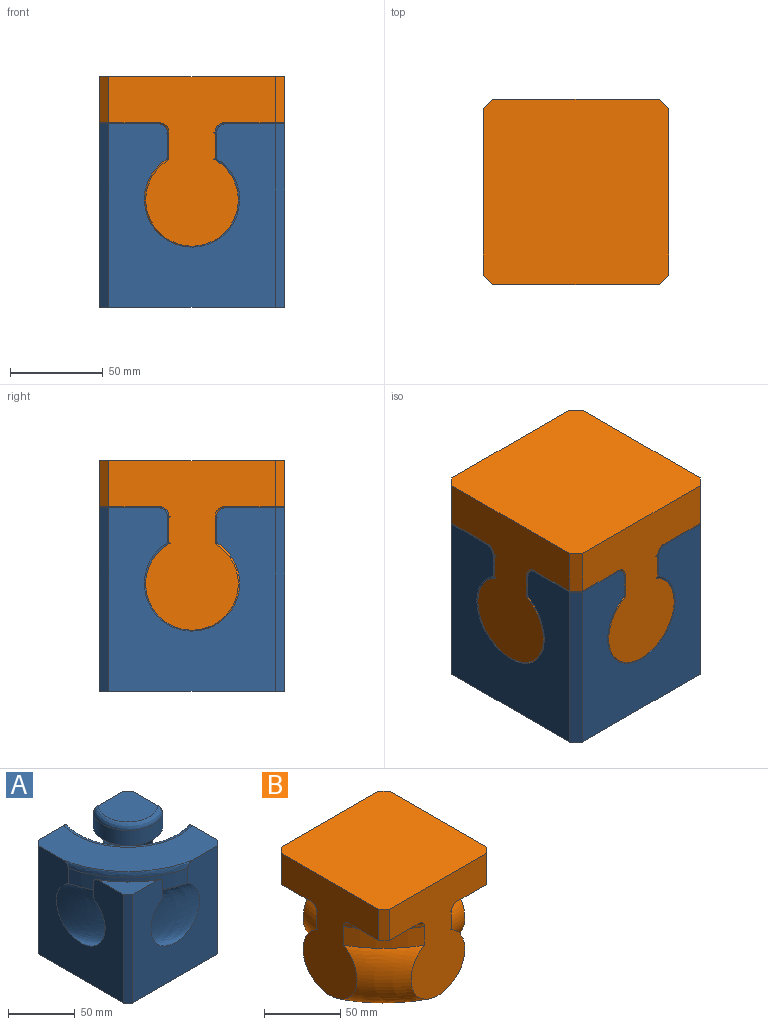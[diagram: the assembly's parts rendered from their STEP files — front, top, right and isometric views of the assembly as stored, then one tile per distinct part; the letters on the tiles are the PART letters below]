
ASSEMBLY  parts=2 mates=1
PART A: 23 faces, bbox 119.4x147.5x99.3 mm
  f0: plane 99.25x90mm, normal (0,1,0), area 6407.5mm2, adj f2,f10,f11,f12,f13,f14,f15,f16
  f1: plane 99.25x90mm, normal (0,-1,0), area 6405.8mm2, adj f2,f5,f6,f7,f8,f9,f17,f18
  f2: plane 100x100mm, normal (0,0,-1), area 9950mm2, adj f0,f1,f3,f4,f19,f20,f21,f22
  f3: plane 99.25x90mm, normal (1,0,0), area 6405.8mm2, adj f2,f10,f11,f12,f14,f15,f16,f17
  f4: plane 99.25x90mm, normal (-1,0,0), area 6405.9mm2, adj f2,f5,f6,f7,f8,f9,f17,f18
  f5: revolved ~41.04x39.31mm, area 308mm2, adj f1,f4,f6,f18
  f6: cylinder r=97.74mm len=36.75mm, axis (0,0,1), area 727.1mm2, adj f1,f4,f5,f7
  f7: revolved ~126.01x95.15mm, area 7683.8mm2, adj f1,f4,f6,f8
  f8: cylinder r=87.74mm len=63.25mm, axis (0,0,1), area 1297.3mm2, adj f1,f4,f7,f9
  f9: revolved ~72.88x70.15mm, area 505.8mm2, adj f1,f4,f8,f17
  f10: revolved ~73.16x70.32mm, area 865.8mm2, adj f0,f3,f11,f17
  f11: cylinder r=50.53mm len=65.53mm, axis (0,0,1), area 1518mm2, adj f0,f3,f10,f12
  f12: revolved ~125.04x77.52mm, area 12006mm2, adj f0,f3,f11,f13,f14
  f13: plane 7.92x0.28mm, normal (-0.91,0.42,0), area 1.6mm2, adj f0,f12
  f14: cylinder r=26.42mm len=41.42mm, axis (0,0,1), area 1014.5mm2, adj f0,f3,f12,f15
  f15: revolved ~46.37x41.42mm, area 502.3mm2, adj f0,f3,f14,f16
  f16: plane 37.48x37.48mm, normal (0,0,1), area 1230mm2, adj f0,f3,f15,f21
  f17: plane 100x100mm, normal (0,0,1), area 4340.4mm2, adj f0,f1,f3,f4,f9,f10,f20,f22
  f18: plane 31.75x31.75mm, normal (0,0,1), area 415.2mm2, adj f1,f4,f5,f19
  f19: plane 99.25x5mm, normal (-0.71,-0.71,0), area 701.8mm2, adj f1,f2,f4,f18
  f20: plane 99.25x5mm, normal (-0.71,0.71,0), area 701.8mm2, adj f0,f2,f4,f17
  f21: plane 99.25x5mm, normal (0.71,0.71,0), area 701.8mm2, adj f0,f2,f3,f16
  f22: plane 99.25x5mm, normal (0.71,-0.71,0), area 701.8mm2, adj f1,f2,f3,f17
PART B: 29 faces, bbox 119x146.8x91.7 mm
  f0: cylinder r=27.04mm len=18.52mm, axis (0,0,1), area 291.5mm2, adj f1,f4,f20,f27
  f1: revolved ~24.31x9.54mm, area 142mm2, adj f0,f17,f20,f27
  f2: revolved ~21.82x7.1mm, area 157.7mm2, adj f3,f15,f20,f27
  f3: cylinder r=49.81mm len=19.49mm, axis (0,0,1), area 296mm2, adj f2,f4,f20,f27
  f4: revolved ~75.55x51.74mm, area 2899mm2, adj f0,f3,f20,f27
  f5: revolved ~123.59x93.96mm, area 7490.6mm2, adj f7,f8,f16,f18
  f6: revolved ~41.76x40.12mm, area 313.9mm2, adj f7,f16,f18,f19
  f7: cylinder r=97.37mm len=37.5mm, axis (0,0,1), area 805.7mm2, adj f5,f6,f16,f18
  f8: cylinder r=87.93mm len=62.5mm, axis (0,0,1), area 1389.2mm2, adj f5,f9,f16,f18
  f9: revolved ~72.09x69.48mm, area 500.9mm2, adj f8,f15,f16,f18
  f10: cylinder r=27.04mm len=19.93mm, axis (0,0,1), area 312.9mm2, adj f11,f14,f22,f27
  f11: revolved ~26.84x9.54mm, area 151.6mm2, adj f10,f17,f22,f27
  f12: revolved ~28.04x7.1mm, area 178.6mm2, adj f13,f15,f22,f27
  f13: cylinder r=49.81mm len=22.1mm, axis (0,0,1), area 335.4mm2, adj f12,f14,f22,f27
  f14: revolved ~76.99x71.01mm, area 3159.3mm2, adj f10,f13,f22,f27
  f15: plane 100x100mm, normal (0,0,-1), area 2740.6mm2, adj f2,f9,f12,f16,f18,f20,f22,f24
  f16: plane 91.65x90mm, normal (0,-1,0), area 4667.6mm2, adj f5,f6,f7,f8,f9,f15,f19,f21
  f17: plane 38.05x38.05mm, normal (0,0,-1), area 1186.5mm2, adj f1,f11,f20,f22,f25,f27
  f18: plane 91.66x90mm, normal (-1,0,0), area 4667.6mm2, adj f5,f6,f7,f8,f9,f15,f19,f21
  f19: plane 32.5x32.5mm, normal (0,0,-1), area 433.3mm2, adj f6,f16,f18,f23
  f20: plane 91.65x90mm, normal (1,0,0), area 4667.6mm2, adj f0,f1,f2,f3,f4,f15,f17,f21
  f21: plane 100x100mm, normal (0,0,1), area 9950mm2, adj f16,f18,f20,f22,f23,f24,f25,f26
  f22: plane 91.66x90mm, normal (0,1,0), area 4668.5mm2, adj f10,f11,f12,f13,f14,f15,f17,f21
  f23: plane 25x5mm, normal (-0.71,-0.71,0), area 176.8mm2, adj f16,f18,f19,f21
  f24: plane 25x5mm, normal (-0.71,0.71,0), area 176.8mm2, adj f15,f18,f21,f22
  f25: plane 25x5mm, normal (0.71,0.71,0), area 176.8mm2, adj f17,f20,f21,f22
  f26: plane 25x5mm, normal (0.71,-0.71,0), area 176.8mm2, adj f15,f16,f20,f21
  f27: cylinder r=33.05mm len=85.95mm, axis (0,0,-1), area 8703.1mm2, adj f0,f1,f2,f3,f4,f10,f11,f12
  f28: plane 66.1x66.1mm, normal (0,0,-1), area 3431.9mm2, adj f27
PLACE A at identity
PLACE B t=(0,0,-0.25)mm
MATE revolute B.f0 <-> A.f6  axis (0,0,-1) through (35,85,37.25)mm
